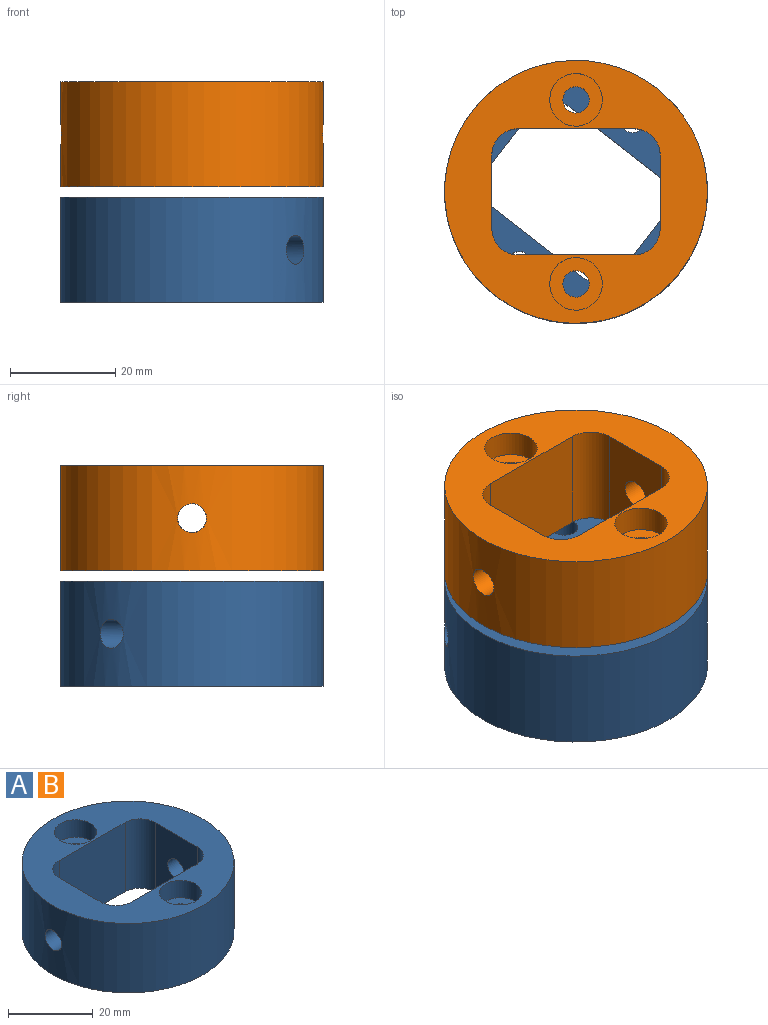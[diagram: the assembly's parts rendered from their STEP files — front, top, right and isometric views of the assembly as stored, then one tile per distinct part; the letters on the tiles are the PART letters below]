
ASSEMBLY  parts=2 mates=1
PART A: 19 faces, bbox 50x50x20 mm
  f0: cylinder r=25mm len=50mm, axis (0,0,-1), area 3093.9mm2, adj f5,f6,f13,f14
  f1: plane 20x14mm, normal (1,0,0), area 256.2mm2, adj f5,f6,f14,f15,f18
  f2: plane 22x20mm, normal (0,-1,0), area 440mm2, adj f5,f6,f15,f16
  f3: plane 20x14mm, normal (-1,0,0), area 256.2mm2, adj f5,f6,f13,f16,f17
  f4: plane 22x20mm, normal (0,1,0), area 440mm2, adj f5,f6,f17,f18
  f5: plane 50x50mm, normal (0,0,1), area 1059.9mm2, adj f0,f1,f2,f3,f4,f9,f12,f15
  f6: plane 50x50mm, normal (0,0,-1), area 1177.7mm2, adj f0,f1,f2,f3,f4,f7,f10,f15
  f7: cylinder r=2.5mm len=15mm, axis (0,0,1), area 235.6mm2, adj f6,f8
  f8: plane 10x10mm, normal (0,0,1), area 58.9mm2, adj f7,f9
  f9: cylinder r=5mm len=10mm, axis (0,0,1), area 157.1mm2, adj f5,f8
  f10: cylinder r=2.5mm len=15mm, axis (0,0,1), area 235.6mm2, adj f6,f11
  f11: plane 10x10mm, normal (0,0,1), area 58.9mm2, adj f10,f12
  f12: cylinder r=5mm len=10mm, axis (0,0,1), area 157.1mm2, adj f5,f11
  f13: cylinder r=2.75mm len=9mm, axis (-1,0,0), area 154.2mm2, adj f0,f3
  f14: cylinder r=2.75mm len=9mm, axis (-1,0,0), area 154.2mm2, adj f0,f1
  f15: cylinder r=5mm len=20mm, axis (0,0,1), area 157.1mm2, adj f1,f2,f5,f6
  f16: cylinder r=5mm len=20mm, axis (0,0,-1), area 157.1mm2, adj f2,f3,f5,f6
  f17: cylinder r=5mm len=20mm, axis (0,0,1), area 157.1mm2, adj f3,f4,f5,f6
  f18: cylinder r=5mm len=20mm, axis (0,0,-1), area 157.1mm2, adj f1,f4,f5,f6
PART B: same geometry as A
PLACE A rot(axis=(0.95,-0.32,0),180deg) t=(1.59,-0.93,-14.77)mm
PLACE B t=(1.59,-0.93,-12.77)mm fixed
MATE revolute A.f0 <-> B.f0  axis (0,0,1) through (1.59,-0.93,-14.77)mm
